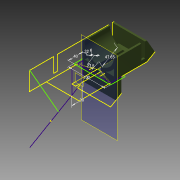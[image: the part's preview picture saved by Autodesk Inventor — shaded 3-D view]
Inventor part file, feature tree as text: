
AUTODESK INVENTOR PART (.ipt)
format: ipt  version: 2013 (Build 170138000, 138)  size: 290,816 bytes
history: native  units: mm
features: sketch x16, extrude x10, other x3, hole x1
ambient origin geometry x8: Origin, YZ Plane, XZ Plane, XY Plane, X Axis, Y Axis, Z Axis, Center Point
feature tree (30):
  other  "ソリッド1"
  extrude  "押し出し1"  Depth=90.0mm
  extrude  "押し出し2"  Depth=50.0mm
  extrude  "押し出し3"  Depth=5.0mm
  extrude  "押し出し4"  Depth=85.0mm
  extrude  "押し出し6"  Depth=5.0mm
  sketch  "スケッチ9"
  hole  "穴1"  [1 undecoded]
  extrude  "押し出し12"  Depth=10.0mm
  sketch  "スケッチ19"
  sketch  "スケッチ20"
  other  "作業平面5"
  extrude  "押し出し13"  Depth=90.0mm
  other  "作業平面6"
  extrude  "押し出し14"  Depth=230.0mm TaperAngle=0.0deg
  extrude  "押し出し15"  Depth=225.0mm TaperAngle=0.0deg
  sketch  "スケッチ24"
  sketch  "スケッチ25"
  extrude  "押し出し16"  Depth=5.0mm TaperAngle=0.0deg
  sketch  "スケッチ1"
  sketch  "スケッチ2"
  sketch  "スケッチ3"
  sketch  "スケッチ4"
  sketch  "スケッチ6"
  sketch  "スケッチ11"
  sketch  "スケッチ18"
  sketch  "スケッチ21"
  sketch  "スケッチ22"
  sketch  "スケッチ23"
  sketch  "スケッチ26"
note: 1 required parameter value undecoded (feature->parameter linkage not recoverable at this tier; creation-order binding heuristic only, values carry confidence <= 0.55)
